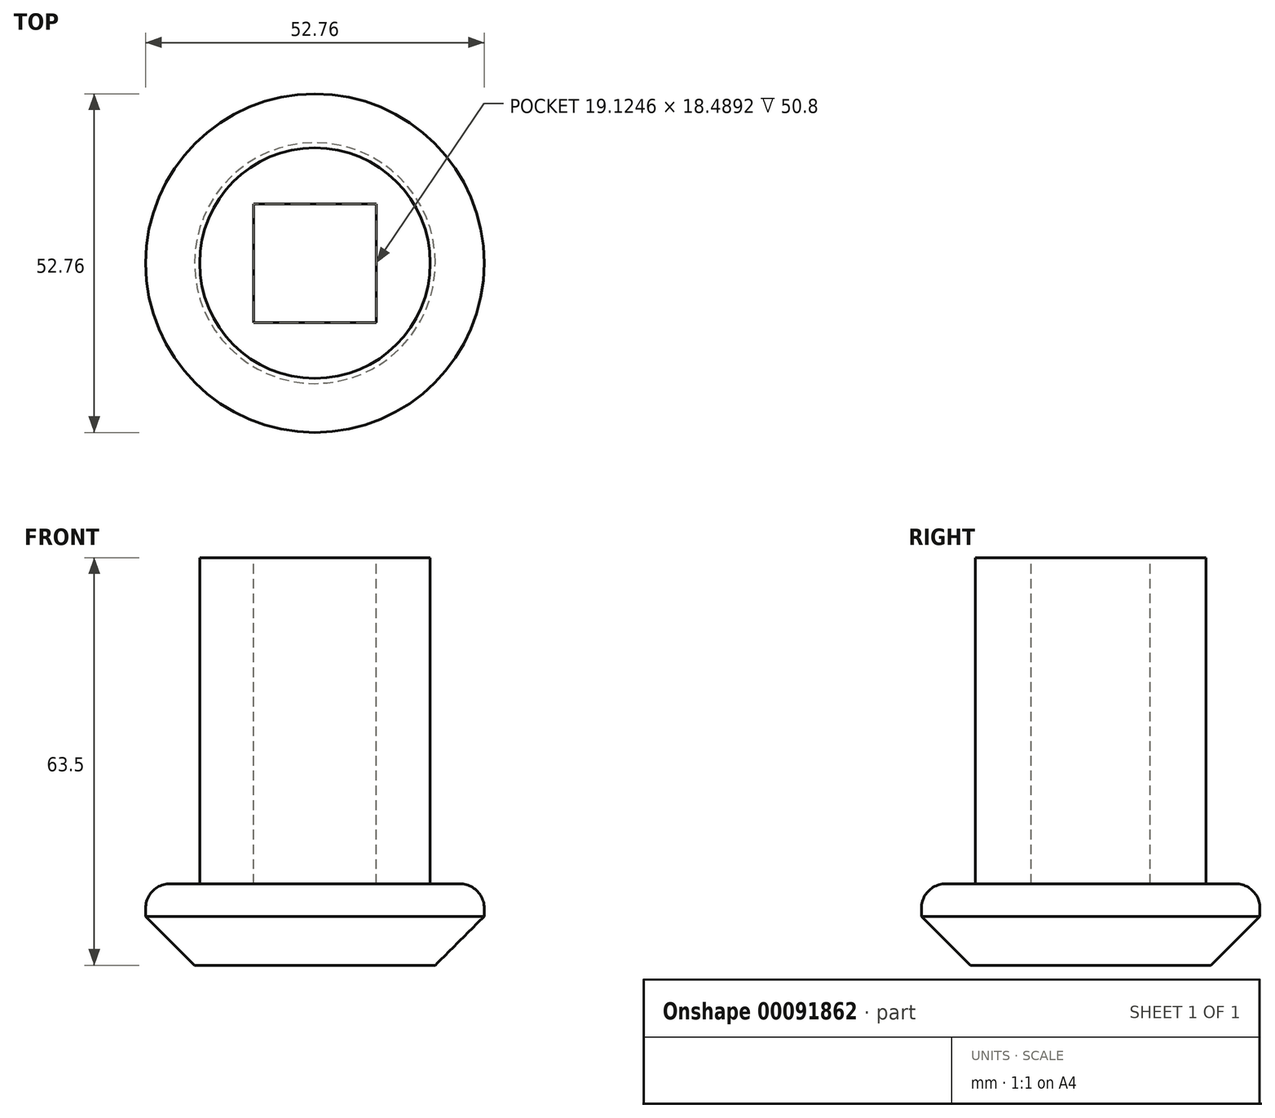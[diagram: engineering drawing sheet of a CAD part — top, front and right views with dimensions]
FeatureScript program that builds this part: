
annotation { "Feature Type Name" : "Feature", "Feature Type Description" : "" }
export const myFeature = defineFeature(function(context is Context, id is Id, definition is map)
    precondition{}
    {
        {
            var Q0;
            Q0=qCreatedBy(makeId("Top.planeOp"),FACE);
            var sketch = newSketch(context, id + "F0", { "sketchPlane" : qUnion([Q0])});
            skCircle(sketch, "E0", {"center": v(0, 0) * mm, "radius": 26.38 * mm});
            skSolve(sketch);
        }
        {
            var Q0;
            Q0=makeQuery(id+"F0.imprint","IMPRINT",FACE,{"disambiguationData":[TD([[makeQuery(id+"F0.imprint","IMPRINT",EDGE,{"derivedFrom":sQuery(id+"F0.wireOp",EDGE,"E0")}),1.0]])]});
            extrude(context, id + "F1", {"entities" : qUnion([Q0]), "oppositeDirection" : true, "depth" : 12.7 * mm});
        }
        {
            var Q0;
            Q0=makeQuery(id+"F1.opExtrude","CAP_EDGE",EDGE,{"disambiguationData":[OSD([sQuery(id+"F0.wireOp",EDGE,"E0")])],"isStart":true});
            fillet(context, id + "F2", {"entities" : qUnion([Q0]), "radius" : 3.8 * mm, "tangentPropagation" : true, "allowEdgeOverflow" : false});
        }
        {
            var Q0;
            Q0=makeQuery(id+"F1.opExtrude","CAP_EDGE",EDGE,{"disambiguationData":[OSD([sQuery(id+"F0.wireOp",EDGE,"E0")])],"isStart":false});
            chamfer(context, id + "F3", {"entities" : qUnion([Q0]), "width" : 7.62 * mm, "tangentPropagation" : true});
        }
        {
            var Q0;
            Q0=makeQuery(id+"F1.opExtrude","CAP_FACE",FACE,{"disambiguationData":[OSD([sQuery(id+"F0.wireOp",EDGE,"E0")])],"isStart":true});
            var sketch = newSketch(context, id + "F4", { "sketchPlane" : qUnion([Q0])});
            skCircle(sketch, "E1", {"center": v(0, 0) * mm, "radius": 17.96 * mm});
            skSolve(sketch);
        }
        {
            var Q0;
            Q0=makeQuery(id+"F4.imprint","IMPRINT",FACE,{"disambiguationData":[TD([[makeQuery(id+"F4.imprint","IMPRINT",EDGE,{"derivedFrom":sQuery(id+"F4.wireOp",EDGE,"E1")}),1.0]])]});
            extrude(context, id + "F5", {"entities" : qUnion([Q0]), "operationType" : NewBodyOperationType.ADD, "depth" : 50.8 * mm});
        }
        {
            var Q0;
            Q0=makeQuery(id+"F5.opExtrude","CAP_FACE",FACE,{"disambiguationData":[OSD([sQuery(id+"F4.wireOp",EDGE,"E1")])],"isStart":false});
            var sketch = newSketch(context, id + "F6", { "sketchPlane" : qUnion([Q0])});
            skLineSegment(sketch, "E2.bottom", {"start": v(-9.56, -9.24) * mm, "end": v(9.56, -9.24) * mm});
            skLineSegment(sketch, "E2.top", {"start": v(-9.56, 9.24) * mm, "end": v(9.56, 9.24) * mm});
            skLineSegment(sketch, "E2.left", {"start": v(-9.56, -9.24) * mm, "end": v(-9.56, 9.24) * mm});
            skLineSegment(sketch, "E2.right", {"start": v(9.56, -9.24) * mm, "end": v(9.56, 9.24) * mm});
            skPoint(sketch, "E2.middle", {"position": v(0, 0) * mm});
            skSolve(sketch);
        }
        {
            var Q0;
            Q0=makeQuery(id+"F6.imprint","IMPRINT",FACE,{"disambiguationData":[TD([[makeQuery(id+"F6.imprint","IMPRINT",EDGE,{"derivedFrom":sQuery(id+"F6.wireOp",EDGE,"E2.bottom")}),1.0]])]});
            extrude(context, id + "F7", {"entities" : qUnion([Q0]), "operationType" : NewBodyOperationType.REMOVE, "oppositeDirection" : true, "depth" : 50.8 * mm});
        }
    });
